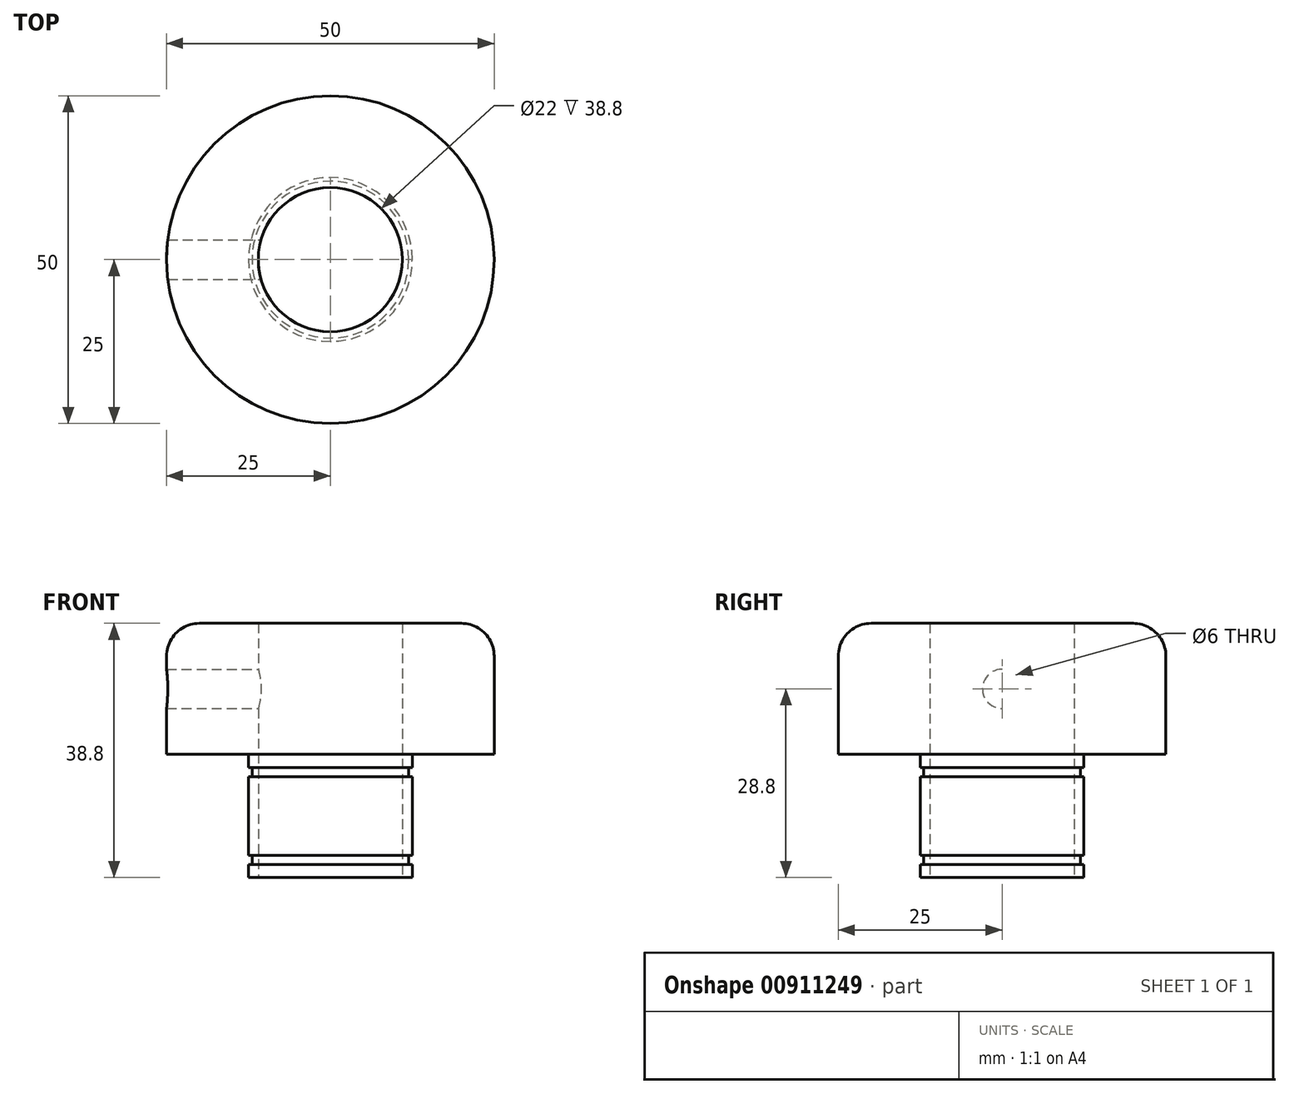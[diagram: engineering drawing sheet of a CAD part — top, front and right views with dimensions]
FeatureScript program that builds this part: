
annotation { "Feature Type Name" : "Feature", "Feature Type Description" : "" }
export const myFeature = defineFeature(function(context is Context, id is Id, definition is map)
    precondition{}
    {
        {
            var Q0;
            Q0=qCreatedBy(makeId("Right.planeOp"),FACE);
            var sketch = newSketch(context, id + "F0", { "sketchPlane" : qUnion([Q0])});
            skLineSegment(sketch, "E0", {"start": v(-11, 0) * mm, "end": v(-11, 38.8) * mm});
            skLineSegment(sketch, "E1", {"start": v(-11, 38.8) * mm, "end": v(-25, 38.8) * mm});
            skLineSegment(sketch, "E2", {"start": v(-25, 38.8) * mm, "end": v(-25, 18.8) * mm});
            skLineSegment(sketch, "E3", {"start": v(-25, 18.8) * mm, "end": v(-12.5, 18.8) * mm});
            skLineSegment(sketch, "E4", {"start": v(-12.5, 3.4) * mm, "end": v(-11.95, 3.4) * mm});
            skLineSegment(sketch, "E5", {"start": v(-11.95, 3.4) * mm, "end": v(-11.95, 2) * mm});
            skLineSegment(sketch, "E6", {"start": v(-11.95, 2) * mm, "end": v(-12.5, 2) * mm});
            skLineSegment(sketch, "E7", {"start": v(-12.5, 2) * mm, "end": v(-12.5, 0) * mm});
            skLineSegment(sketch, "E8", {"start": v(-12.5, 0) * mm, "end": v(-11, 0) * mm});
            skLineSegment(sketch, "E9", {"start": v(0, 0) * mm, "end": v(0, 39.07) * mm});
            skLineSegment(sketch, "E10", {"start": v(-12.5, 18.8) * mm, "end": v(-12.5, 16.8) * mm});
            skLineSegment(sketch, "E11", {"start": v(-12.5, 16.8) * mm, "end": v(-11.95, 16.8) * mm});
            skLineSegment(sketch, "E12", {"start": v(-11.95, 16.8) * mm, "end": v(-11.95, 15.4) * mm});
            skLineSegment(sketch, "E13", {"start": v(-11.95, 15.4) * mm, "end": v(-12.5, 15.4) * mm});
            skLineSegment(sketch, "E14", {"start": v(-12.5, 15.4) * mm, "end": v(-12.5, 3.4) * mm});
            skSolve(sketch);
        }
        {
            var Q0;
            Q0=makeQuery(id+"F0.imprint","IMPRINT",FACE,{"disambiguationData":[TD([[makeQuery(id+"F0.imprint","IMPRINT",EDGE,{"derivedFrom":sQuery(id+"F0.wireOp",EDGE,"E0")}),1.0]])]});
            var Q1;
            Q1=sQuery(id+"F0.wireOp",EDGE,"E9");
            revolve(context, id + "F1", {"surfaceOperationType" : NewSurfaceOperationType.NEW, "entities" : qUnion([Q0]), "axis" : qUnion([Q1]), "revolveType" : RevolveType.FULL});
        }
        {
            var Q0;
            Q0=makeQuery(id+"F1.opRevolve","SWEPT_EDGE",EDGE,{"disambiguationData":[OSD([sQuery(id+"F0.wireOp",EDGE,"E1"),sQuery(id+"F0.wireOp",EDGE,"E2")])]});
            fillet(context, id + "F2", {"entities" : qUnion([Q0]), "radius" : 5 * mm, "tangentPropagation" : true, "allowEdgeOverflow" : false});
        }
        {
            var Q0;
            Q0=qCreatedBy(makeId("Right.planeOp"),FACE);
            var sketch = newSketch(context, id + "F3", { "sketchPlane" : qUnion([Q0])});
            skPoint(sketch, "E15", {"position": v(0, 28.8) * mm});
            skSolve(sketch);
        }
        {
            var Q0;
            Q0=sQuery(id+"F3.wireOp",VERTEX,"E15");
            var Q1;
            Q1=makeQuery(id+"F1.opRevolve","SWEPT_BODY",BODY,{"disambiguationData":[OSD([sQuery(id+"F0.wireOp",EDGE,"E0"),sQuery(id+"F0.wireOp",EDGE,"E1"),sQuery(id+"F0.wireOp",EDGE,"E2"),sQuery(id+"F0.wireOp",EDGE,"E3"),sQuery(id+"F0.wireOp",EDGE,"xpJyYUbx-97xg-leqJ-W7wg-VAUFvncfsA3P"),sQuery(id+"F0.wireOp",EDGE,"E4"),sQuery(id+"F0.wireOp",EDGE,"E5"),sQuery(id+"F0.wireOp",EDGE,"E6"),sQuery(id+"F0.wireOp",EDGE,"E7"),sQuery(id+"F0.wireOp",EDGE,"E8")])]});
            hole(context, id + "F4", {"style" : HoleStyle.SIMPLE, "endStyle" : HoleEndStyle.THROUGH, "holeDiameter" : 6 * mm, "majorDiameter" : 5 * mm, "isTappedThrough" : true, "tappedDepth" : 12 * mm, "tapClearance" : 3, "locations" : qUnion([Q0]), "scope" : qUnion([Q1])});
        }
    });
